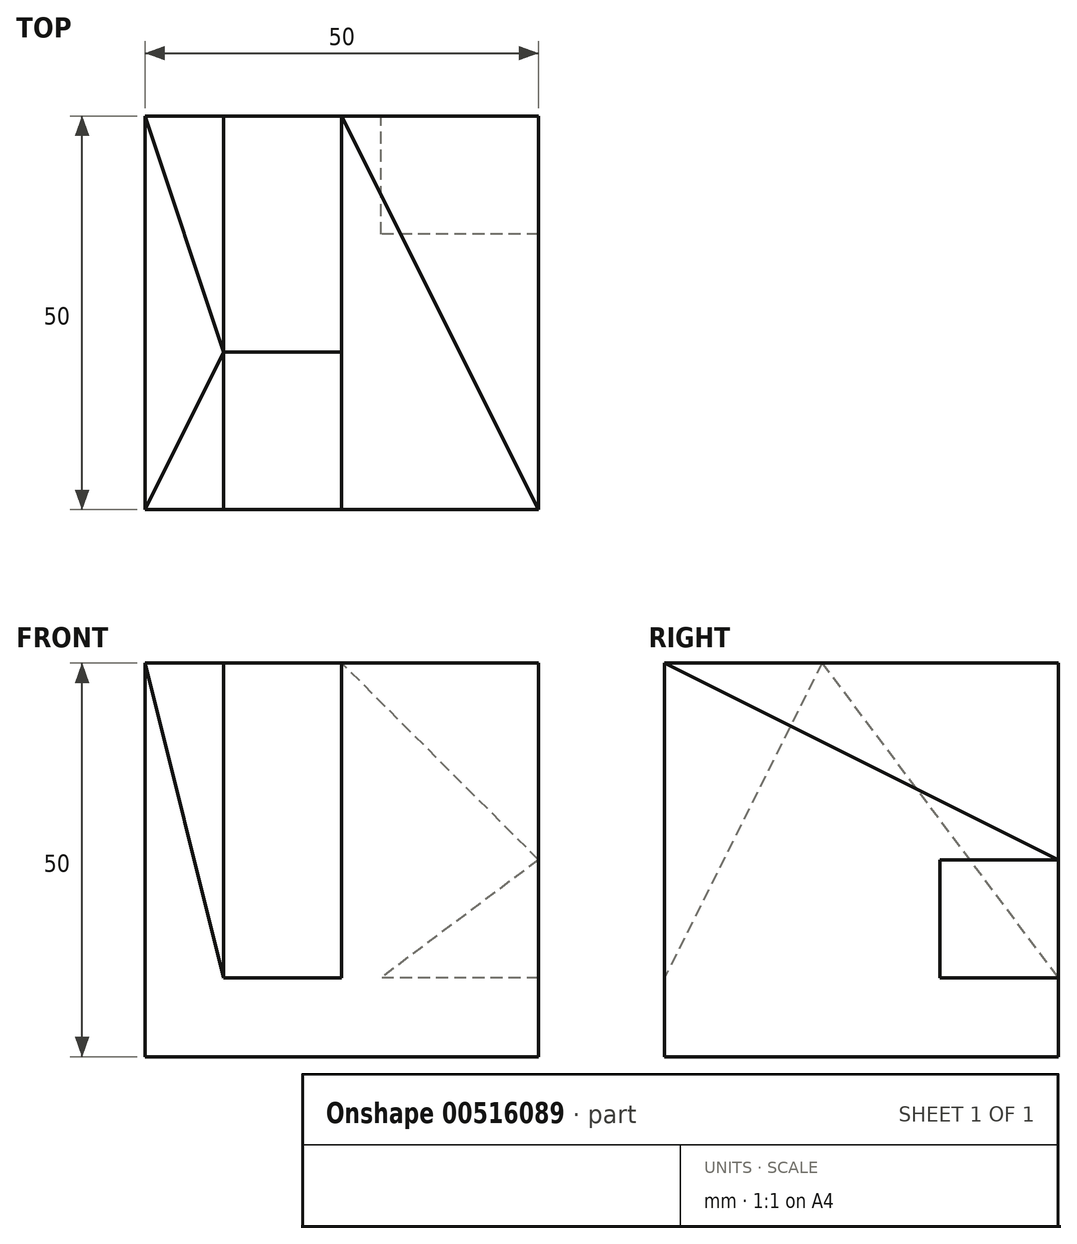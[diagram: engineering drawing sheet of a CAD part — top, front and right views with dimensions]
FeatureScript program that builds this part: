
annotation { "Feature Type Name" : "Feature", "Feature Type Description" : "" }
export const myFeature = defineFeature(function(context is Context, id is Id, definition is map)
    precondition{}
    {
        {
            var Q0;
            Q0=qCreatedBy(makeId("Top.planeOp"),FACE);
            var sketch = newSketch(context, id + "F0", { "sketchPlane" : qUnion([Q0])});
            skLineSegment(sketch, "E0.bottom", {"start": v(0, 0) * mm, "end": v(50, 0) * mm});
            skLineSegment(sketch, "E0.top", {"start": v(0, 50) * mm, "end": v(50, 50) * mm});
            skLineSegment(sketch, "E0.left", {"start": v(0, 0) * mm, "end": v(0, 50) * mm});
            skLineSegment(sketch, "E0.right", {"start": v(50, 0) * mm, "end": v(50, 50) * mm});
            skSolve(sketch);
        }
        {
            var Q0;
            Q0 = qSketchRegion(id + "F0", true);
            extrude(context, id + "F1", {"entities" : qUnion([Q0]), "depth" : 50 * mm, "offsetDistance" : 25 * mm});
        }
        {
            var Q0;
            Q0=makeQuery(id+"F1.opExtrude","CAP_FACE",FACE,{"disambiguationData":[OSD([sQuery(id+"F0.wireOp",EDGE,"E0.bottom"),sQuery(id+"F0.wireOp",EDGE,"E0.top"),sQuery(id+"F0.wireOp",EDGE,"E0.left"),sQuery(id+"F0.wireOp",EDGE,"E0.right")])],"isStart":false});
            var sketch = newSketch(context, id + "F2", { "sketchPlane" : qUnion([Q0])});
            skLineSegment(sketch, "E1", {"start": v(0, 0) * mm, "end": v(10, 0) * mm});
            skLineSegment(sketch, "E2", {"start": v(10, 0) * mm, "end": v(25, 0) * mm});
            skLineSegment(sketch, "E3", {"start": v(10, 0) * mm, "end": v(10, 50) * mm});
            skLineSegment(sketch, "E4", {"start": v(25, 0) * mm, "end": v(25, 50) * mm});
            skLineSegment(sketch, "E5", {"start": v(25, 50) * mm, "end": v(10, 50) * mm});
            skLineSegment(sketch, "E6", {"start": v(10, 0) * mm, "end": v(10, 20) * mm});
            skLineSegment(sketch, "E7", {"start": v(10, 20) * mm, "end": v(25, 20) * mm});
            skSolve(sketch);
        }
        {
            var Q0;
            Q0=makeQuery(id+"F1.opExtrude","SWEPT_FACE",FACE,{"disambiguationData":[OSD([sQuery(id+"F0.wireOp",EDGE,"E0.right")])]});
            var sketch = newSketch(context, id + "F3", { "sketchPlane" : qUnion([Q0])});
            skLineSegment(sketch, "E8", {"start": v(0, 0) * mm, "end": v(0, 10) * mm});
            skLineSegment(sketch, "E9", {"start": v(0, 10) * mm, "end": v(20, 50) * mm});
            skLineSegment(sketch, "E10", {"start": v(0, 10) * mm, "end": v(50, 10) * mm});
            skLineSegment(sketch, "E11", {"start": v(50, 10) * mm, "end": v(20, 50) * mm});
            skSolve(sketch);
        }
        {
            var Q0;
            {var subQ0=sQuery(id+"F2.wireOp",EDGE,"E2");Q0=makeQuery(id+"F2.imprint","IMPRINT",FACE,{"disambiguationData":[TD([[makeQuery(id+"F2.imprint","IMPRINT",EDGE,{"derivedFrom":subQ0}),1.0]])]});}
            var Q1;
            Q1=sQuery(id+"F3.wireOp",EDGE,"E9");
            sweep(context, id + "F4", {"operationType" : NewBodyOperationType.REMOVE, "profiles" : qUnion([Q0]), "path" : qUnion([Q1])});
        }
        {
            var Q0;
            Q0=makeQuery(id+"F1.opExtrude","CAP_FACE",FACE,{"disambiguationData":[OSD([sQuery(id+"F0.wireOp",EDGE,"E0.bottom"),sQuery(id+"F0.wireOp",EDGE,"E0.top"),sQuery(id+"F0.wireOp",EDGE,"E0.left"),sQuery(id+"F0.wireOp",EDGE,"E0.right")])],"isStart":false});
            var sketch = newSketch(context, id + "F5", { "sketchPlane" : qUnion([Q0])});
            skLineSegment(sketch, "E12", {"start": v(10, 20) * mm, "end": v(10, 50) * mm});
            skLineSegment(sketch, "E13", {"start": v(10, 20) * mm, "end": v(25, 20) * mm});
            skLineSegment(sketch, "E14", {"start": v(25, 20) * mm, "end": v(25, 50) * mm});
            skLineSegment(sketch, "E15", {"start": v(25, 50) * mm, "end": v(10, 50) * mm});
            skSolve(sketch);
        }
        {
            var Q0;
            Q0=makeQuery(id+"F1.opExtrude","SWEPT_FACE",FACE,{"disambiguationData":[OSD([sQuery(id+"F0.wireOp",EDGE,"E0.right")])]});
            var sketch = newSketch(context, id + "F6", { "sketchPlane" : qUnion([Q0])});
            skLineSegment(sketch, "E16", {"start": v(0, 0) * mm, "end": v(0, 10) * mm});
            skLineSegment(sketch, "E17", {"start": v(0, 10) * mm, "end": v(50, 10) * mm});
            skLineSegment(sketch, "E18", {"start": v(50, 10) * mm, "end": v(20, 50) * mm});
            skSolve(sketch);
        }
        {
            var Q0;
            Q0=makeQuery(id+"F5.imprint","IMPRINT",FACE,{"disambiguationData":[TD([[makeQuery(id+"F5.imprint","IMPRINT",EDGE,{"derivedFrom":sQuery(id+"F5.wireOp",EDGE,"E12")}),-1.0]])]});
            var Q1;
            Q1=sQuery(id+"F6.wireOp",EDGE,"E18");
            sweep(context, id + "F7", {"operationType" : NewBodyOperationType.REMOVE, "profiles" : qUnion([Q0]), "path" : qUnion([Q1])});
        }
        {
            var Q0;
            Q0=makeQuery(id+"F1.opExtrude","SWEPT_FACE",FACE,{"disambiguationData":[OSD([sQuery(id+"F0.wireOp",EDGE,"E0.top")])]});
            var sketch = newSketch(context, id + "F8", { "sketchPlane" : qUnion([Q0])});
            skLineSegment(sketch, "E19", {"start": v(0, 50) * mm, "end": v(-10, 10) * mm});
            skSolve(sketch);
        }
        {
            var Q0;
            Q0=makeQuery(id+"F7.boolean.opBoolean","COPY",FACE,{"derivedFrom":makeQuery(id+"F7.opSweep","SWEPT_FACE",FACE,{"disambiguationData":[OSD([sQuery(id+"F5.wireOp",EDGE,"E12"),sQuery(id+"F6.wireOp",EDGE,"E18")])]})});
            var Q1;
            Q1=sQuery(id+"F8.wireOp",EDGE,"E19");
            sweep(context, id + "F9", {"operationType" : NewBodyOperationType.REMOVE, "profiles" : qUnion([Q0]), "path" : qUnion([Q1])});
        }
        {
            var Q0;
            {var subQ1=sQuery(id+"F0.wireOp",EDGE,"E0.top");var subQ3=sQuery(id+"F0.wireOp",EDGE,"E0.left");var subQ4=sQuery(id+"F0.wireOp",EDGE,"E0.bottom");Q0=makeQuery(id+"F7.boolean.opBoolean","SPLIT",FACE,{"disambiguationData":[TD([makeQuery(id+"F1.opExtrude","SWEPT_FACE",FACE,{"disambiguationData":[OSD([subQ3])]})])],"derivedFrom":makeQuery(id+"F1.opExtrude","CAP_FACE",FACE,{"disambiguationData":[OSD([subQ4,subQ1,subQ3,sQuery(id+"F0.wireOp",EDGE,"E0.right")])],"isStart":false})});}
            var sketch = newSketch(context, id + "F10", { "sketchPlane" : qUnion([Q0])});
            skLineSegment(sketch, "E20", {"start": v(10, 20) * mm, "end": v(0, 0) * mm});
            skSolve(sketch);
        }
        {
            var Q0;
            Q0=makeQuery(id+"F4.boolean.opBoolean","COPY",FACE,{"derivedFrom":makeQuery(id+"F4.opSweep","SWEPT_FACE",FACE,{"disambiguationData":[OSD([sQuery(id+"F2.wireOp",EDGE,"E6"),sQuery(id+"F3.wireOp",EDGE,"E9")])]})});
            var Q1;
            Q1=sQuery(id+"F10.wireOp",EDGE,"E20");
            sweep(context, id + "F11", {"operationType" : NewBodyOperationType.REMOVE, "profiles" : qUnion([Q0]), "path" : qUnion([Q1])});
        }
        {
            var Q0;
            {var subQ1=sQuery(id+"F0.wireOp",EDGE,"E0.top");var subQ3=sQuery(id+"F0.wireOp",EDGE,"E0.right");var subQ4=sQuery(id+"F0.wireOp",EDGE,"E0.bottom");Q0=makeQuery(id+"F7.boolean.opBoolean","SPLIT",FACE,{"disambiguationData":[TD([makeQuery(id+"F1.opExtrude","SWEPT_FACE",FACE,{"disambiguationData":[OSD([subQ3])]})])],"derivedFrom":makeQuery(id+"F1.opExtrude","CAP_FACE",FACE,{"disambiguationData":[OSD([subQ4,subQ1,sQuery(id+"F0.wireOp",EDGE,"E0.left"),subQ3])],"isStart":false})});}
            var sketch = newSketch(context, id + "F12", { "sketchPlane" : qUnion([Q0])});
            skLineSegment(sketch, "E21", {"start": v(25, 50) * mm, "end": v(50, 0) * mm});
            skSolve(sketch);
        }
        {
            var Q0;
            Q0=makeQuery(id+"F1.opExtrude","SWEPT_FACE",FACE,{"disambiguationData":[OSD([sQuery(id+"F0.wireOp",EDGE,"E0.right")])]});
            var sketch = newSketch(context, id + "F13", { "sketchPlane" : qUnion([Q0])});
            skLineSegment(sketch, "E22", {"start": v(0, 50) * mm, "end": v(50, 25) * mm});
            skSolve(sketch);
        }
        {
            var Q0;
            Q0=makeQuery(id+"F12.imprint","IMPRINT",FACE,{"disambiguationData":[TD([[makeQuery(id+"F12.imprint","IMPRINT",EDGE,{"derivedFrom":sQuery(id+"F12.wireOp",EDGE,"E21")}),1.0]])]});
            var Q1;
            Q1=sQuery(id+"F13.wireOp",EDGE,"E22");
            sweep(context, id + "F14", {"operationType" : NewBodyOperationType.REMOVE, "profiles" : qUnion([Q0]), "path" : qUnion([Q1])});
        }
        {
            var Q0;
            Q0=makeQuery(id+"F1.opExtrude","SWEPT_FACE",FACE,{"disambiguationData":[OSD([sQuery(id+"F0.wireOp",EDGE,"E0.top")])]});
            var sketch = newSketch(context, id + "F15", { "sketchPlane" : qUnion([Q0])});
            skLineSegment(sketch, "E23", {"start": v(-50, 0) * mm, "end": v(-50, 10) * mm});
            skLineSegment(sketch, "E24", {"start": v(-50, 0) * mm, "end": v(-50, 25) * mm});
            skLineSegment(sketch, "E25", {"start": v(-50, 10) * mm, "end": v(-30, 10) * mm});
            skLineSegment(sketch, "E26", {"start": v(-50, 25) * mm, "end": v(-30, 10) * mm});
            skSolve(sketch);
        }
        {
            var Q0;
            Q0 = qSketchRegion(id + "F15", true);
            extrude(context, id + "F16", {"entities" : qUnion([Q0]), "operationType" : NewBodyOperationType.REMOVE, "oppositeDirection" : true, "depth" : 15 * mm, "offsetDistance" : 25 * mm});
        }
    });
